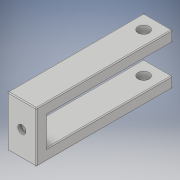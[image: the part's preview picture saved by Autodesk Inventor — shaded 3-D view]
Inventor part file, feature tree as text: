
AUTODESK INVENTOR PART (.ipt)
format: ipt  version: 2017 (Build 210142000, 142)  size: 170,496 bytes
history: native  units: in
note: dims shown in document units (in); Inventor stores cm internally (conversion verified against a paired STEP export)
features: extrude x4, sketch x4, projected_geometry x4, fillet x1
ambient origin geometry x8: Origin, YZ Plane, XZ Plane, XY Plane, X Axis, Y Axis, Z Axis, Center Point
bodies: Solid1 (feature_tree)
feature tree (13):
  extrude  "Extrusion1"  Depth=0.5in
  extrude  "Extrusion2"  Depth=0.5in TaperAngle=0.0deg
  extrude  "Extrusion3"  Depth=0.5in
  extrude  "Extrusion4"  Depth=0.015in TaperAngle=0.0deg
  fillet  "Fillet2"  Radius=2.35in
  sketch  "Sketch1"  dims[d1=2.35in d4=0.5in]
  sketch  "Sketch2"  dims[d6=0.1875in d7=0.5in d8=0.0in]
  projected_geometry  "Projected Loop1"
  sketch  "Sketch3"  dims[d9=0.195in d10=0.5in]
  projected_geometry  "Projected Loop2"
  projected_geometry  "Projected Loop3"
  sketch  "Sketch4"  dims[d11=0.25in d13=1.0in d14=0.0in d15=2.35in d16=0.25in d17=0.375in d18=0.25in d19=0.25in d20=0.125in d21=0.0in d22=0.1875in d23=0.5in d24=0.1875in d25=0.14in d26=1.0in d27=0.0in d29=0.015in]
  projected_geometry  "Projected Loop4"
